# Revit family: Electronics_Commercial-Audio_Biamp_Tabletop-Cable-Grommet_MC-1
name_source: partatom
category: Communication Devices
units: mm (PartAtom-declared; Revit-internal decimal feet)

## family parameters
Cut with Voids When Loaded = No
Host = Face
Maintain Annotation Orientation = No
OmniClass Number = 23.85.10.11.14
Part Type = Normal
Room Calculation Point = No
Round Connector Dimension = Use Diameter
Shared = No

## types (1)
- MC1
    Altitude = 0-6,600 ft (0-2000m) MSL
    Compliance = RoHS Directive (Europe)
    Configurable = Supports up to three cables
    Default Elevation = 4' - 0"
    Description = EasyConnect MC1 Tabletop Cable Grommet
    Diameter = 0' - 4 1/2"
    Height = 0' - 3 1/2"
    Housing Material = Biamp - Plastic - Black
    Humidity = 10-90% relative humidity (non-condensing)
    Included Accessories = Tension ring, Cable ribs, Cable tie holders, Cable bushings, Cable ties, Cable bag, Screws
    Manufacturer = Biamp
    Model = MC1
    Product Documentation Link = https://downloads.biamp.com
    Product Page URL = https://www.biamp.com
    Product data url = https://www.bimobject.com
    Shipping Weight = 0.90 lbf
    Temperature Range = 32 - 104° F (0 – 40° C)
    The maximum outer cable diameter = 0' - 0 1/2"
    URL = https://www.biamp.com
    Weight = 0.50 lbf

## geometry (parser evidence)
native form markers: Sweep x2
no freeform markers — native parametric forms only
